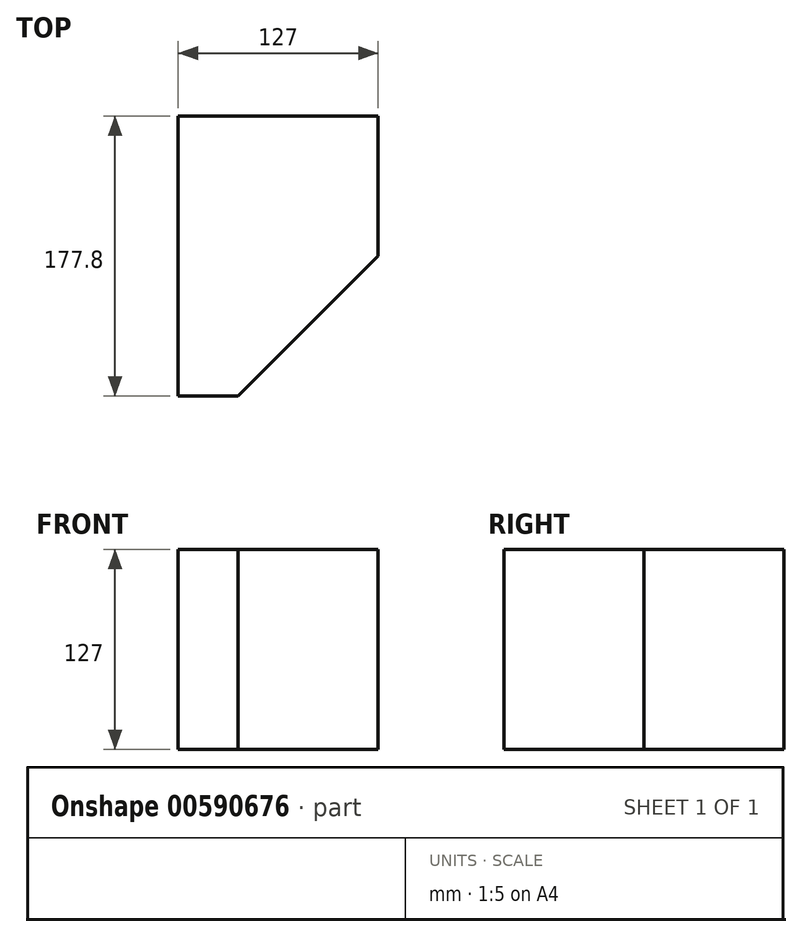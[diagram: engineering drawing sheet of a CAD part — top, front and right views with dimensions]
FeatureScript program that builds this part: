
annotation { "Feature Type Name" : "Feature", "Feature Type Description" : "" }
export const myFeature = defineFeature(function(context is Context, id is Id, definition is map)
    precondition{}
    {
        {
            var Q0;
            Q0=qCreatedBy(makeId("Top.planeOp"),FACE);
            var sketch = newSketch(context, id + "F0", { "sketchPlane" : qUnion([Q0])});
            skLineSegment(sketch, "E0.bottom", {"start": v(0, 0) * mm, "end": v(-127, 0) * mm});
            skLineSegment(sketch, "E0.top", {"start": v(0, -177.8) * mm, "end": v(-127, -177.8) * mm});
            skLineSegment(sketch, "E0.left", {"start": v(0, 0) * mm, "end": v(0, -177.8) * mm});
            skLineSegment(sketch, "E0.right", {"start": v(-127, 0) * mm, "end": v(-127, -177.8) * mm});
            skSolve(sketch);
        }
        {
            var Q0;
            Q0=makeQuery(id+"F0.imprint","IMPRINT",FACE,{"disambiguationData":[TD([[makeQuery(id+"F0.imprint","IMPRINT",EDGE,{"derivedFrom":sQuery(id+"F0.wireOp",EDGE,"E0.bottom")}),1.0]])]});
            extrude(context, id + "F1", {"entities" : qUnion([Q0]), "depth" : 127 * mm, "offsetDistance" : 25.4 * mm});
        }
        {
            var Q0;
            Q0=makeQuery(id+"F1.opExtrude","SWEPT_EDGE",EDGE,{"disambiguationData":[OSD([sQuery(id+"F0.wireOp",EDGE,"E0.top"),sQuery(id+"F0.wireOp",EDGE,"E0.left")])]});
            chamfer(context, id + "F2", {"entities" : qUnion([Q0]), "width" : 88.9 * mm, "tangentPropagation" : true});
        }
    });
